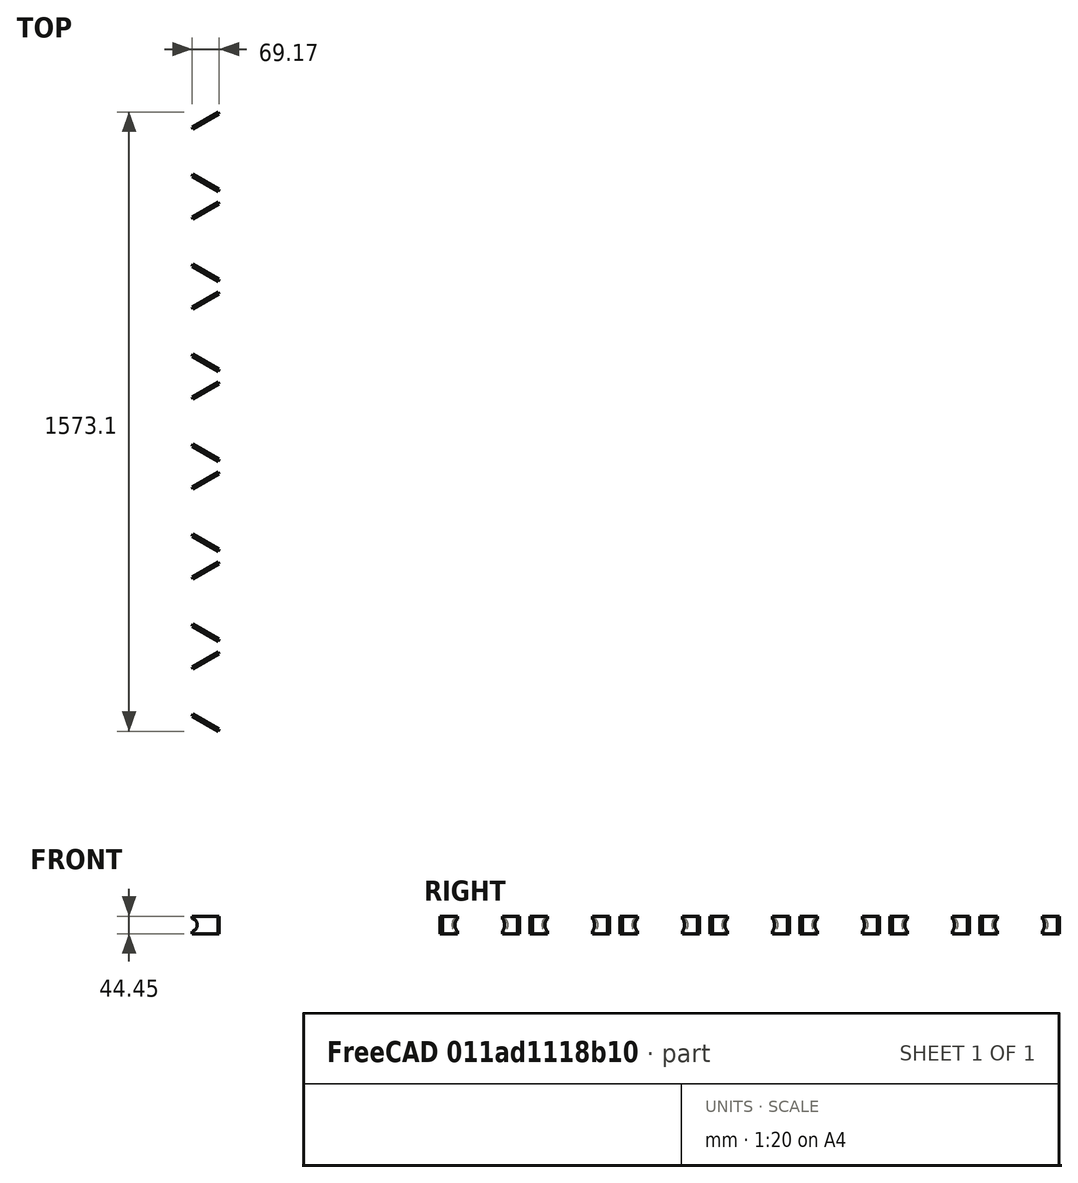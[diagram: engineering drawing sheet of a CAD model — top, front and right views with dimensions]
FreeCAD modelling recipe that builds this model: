
FCSTD DOCUMENT  (FreeCAD 0.17R13522 (Git))
Label: small_gussets
License: CreativeCommons Attribution
LicenseURL: http://creativecommons.org/licenses/by/4.0/
objects: Part::FeaturePython×4, Part::Box×1, Part::Cut×1, Part::Mirroring×1, Part::MultiFuse×1, Part::Feature×1
note: 9 computed .brp shape members not serialized (recipe doc carries the construction recipe); baked Part::Feature solids carry a one-line shape summary decoded from their .brp

FEATURE [Part::FeaturePython] Tube_1_625_sch80_01  label="Tube_1_315_0.133thick"  # a2plus imported part (geometry in sourceFile) (typed FeaturePython)
  Placement = pos=(780.915,0,22.4829) rot=(-0.624695,0,0.780869;3.14159rad)
  fixedPosition = false
  sourceFile = <userpath>/Freecad_Git/Grapples/01_Hardware/Mechanical_Parts/Tube 1.315 0.133 thick for tines.fcstd
  timeLastImport = 1.52609e+09
  updateColors = true
FEATURE [Part::FeaturePython] gussets_01  label="Inside gussets"  # a2plus imported part (geometry in sourceFile) (typed FeaturePython)
  Placement = pos=(780.915,228.6,-21.9671) rot=(0,0,1;0rad)
  fixedPosition = false
  sourceFile = <userpath>/Freecad_Git/Grapples/01_Hardware/Mechanical_Parts/Inside Gussets.fcstd
  timeLastImport = 1.52577e+09
  updateColors = true
FEATURE [Part::Box] Box  label="Cube"
  AttacherType = Attacher::AttachEngine3D
  Height = 44.45
  Length = 76.2
  Placement = pos=(787.4,177.8,0) rot=(0,0,1;0.523599rad)
  Width = 6.35
FEATURE [Part::FeaturePython] Cutout  label="Used for dxf export small gusset"  # WARN: FeaturePython — macro-defined, semantics opaque (R4)
  Base = -> Box
  Tolerance = 0
  Tool = -> Tube_1_625_sch80_01
FEATURE [Part::Cut] Cut
  Base = -> Cutout
  Placement = pos=(0,-120.65,0) rot=(0,0,1;0rad)
  Tool = -> gussets_01
FEATURE [Part::Mirroring] Part__Mirroring  label="Cut (Mirror #1)"
  Base = (0,0,0)
  Normal = (0,1,0)
  Source = -> Cut
FEATURE [Part::MultiFuse] Fusion
  Shapes = -> [Cut,Part__Mirroring]
FEATURE [Part::FeaturePython] Array  # Draft array (typed FeaturePython)
  Angle = 360
  ArrayType = 0
  Axis = (0,0,1)
  Base = -> Fusion
  Center = (0,0,0)
  Fuse = false
  IntervalAxis = (0,0,0)
  IntervalX = (1,0,0)
  IntervalY = (0,228.6,0)
  IntervalZ = (0,0,0)
  NumberPolar = 1
  NumberX = 1
  NumberY = 7
  NumberZ = 1
FEATURE [Part::Feature] Face003  label="face used for dxf cutting (the inside one)"
  Placement = pos=(0,-120.65,0) rot=(0,0,-1;0.523599rad)
  shape: bbox 76.2 x 2e-07 x 44.45 mm, 1 faces, 0 solids (baked)
